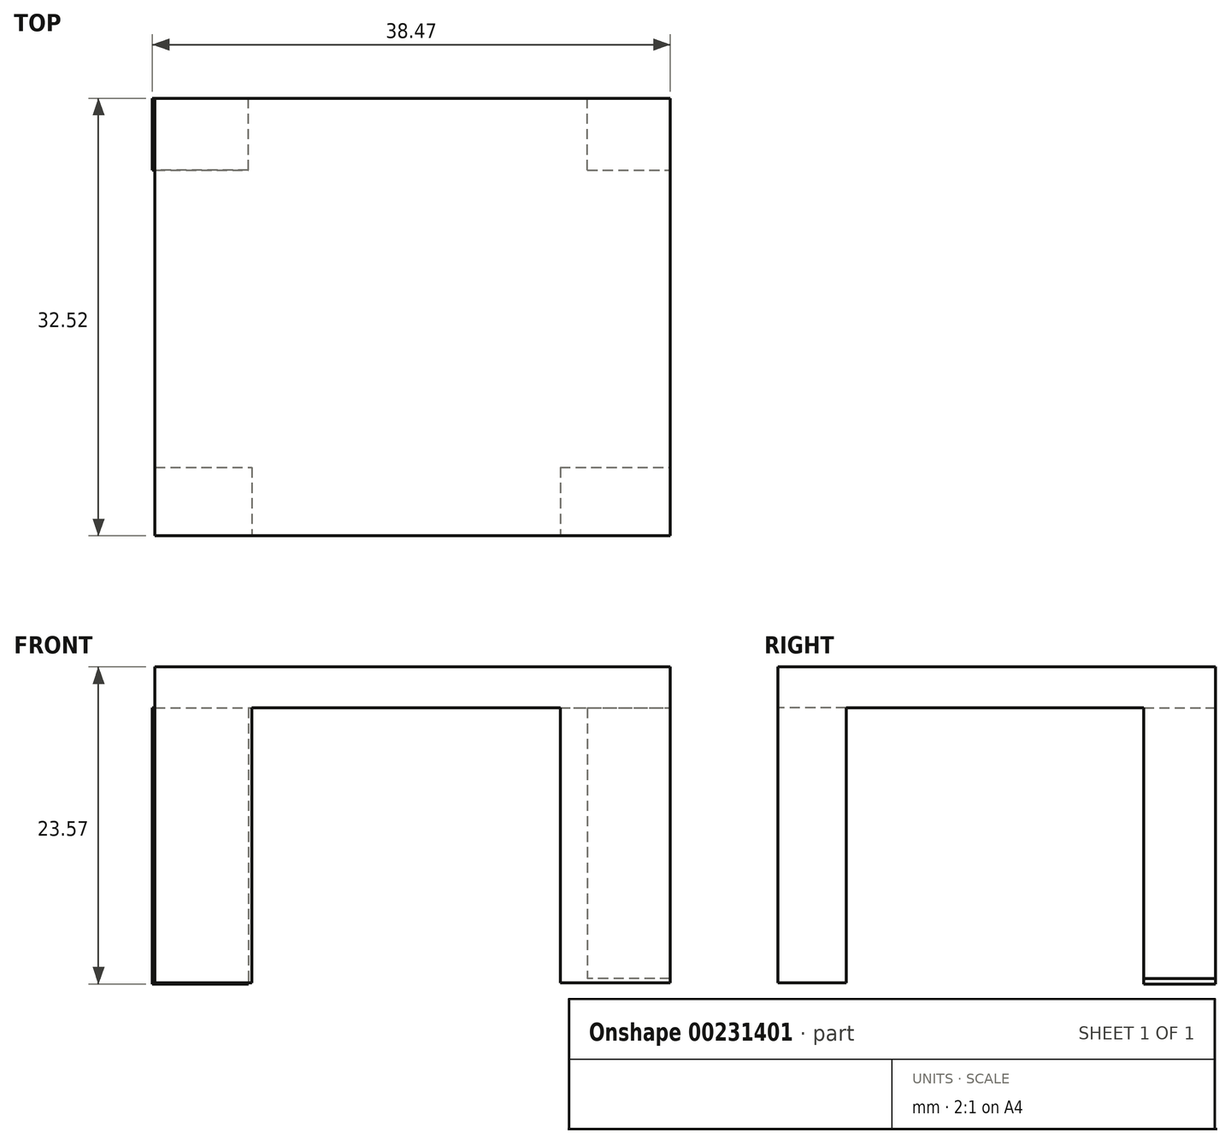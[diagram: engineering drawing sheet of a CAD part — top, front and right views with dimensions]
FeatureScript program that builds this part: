
annotation { "Feature Type Name" : "Feature", "Feature Type Description" : "" }
export const myFeature = defineFeature(function(context is Context, id is Id, definition is map)
    precondition{}
    {
        {
            var Q0;
            Q0=qCreatedBy(makeId("Top.planeOp"),FACE);
            var sketch = newSketch(context, id + "F0", { "sketchPlane" : qUnion([Q0])});
            skLineSegment(sketch, "E0.bottom", {"start": v(-51.75, -22.5) * mm, "end": v(-13.48, -22.5) * mm});
            skLineSegment(sketch, "E0.top", {"start": v(-51.75, -55.03) * mm, "end": v(-13.48, -55.03) * mm});
            skLineSegment(sketch, "E0.left", {"start": v(-51.75, -22.5) * mm, "end": v(-51.75, -55.03) * mm});
            skLineSegment(sketch, "E0.right", {"start": v(-13.48, -22.5) * mm, "end": v(-13.48, -55.03) * mm});
            skSolve(sketch);
        }
        {
            var Q0;
            Q0 = qSketchRegion(id + "F0", true);
            extrude(context, id + "F1", {"entities" : qUnion([Q0]), "depth" : 3.05 * mm});
        }
        {
            var Q0;
            Q0=makeQuery(id+"F1.opExtrude","SWEPT_FACE",FACE,{"disambiguationData":[OSD([sQuery(id+"F0.wireOp",EDGE,"E0.bottom")])]});
            var sketch = newSketch(context, id + "F2", { "sketchPlane" : qUnion([Q0])});
            skLineSegment(sketch, "E1.bottom", {"start": v(13.48, 0) * mm, "end": v(19.63, 0) * mm});
            skLineSegment(sketch, "E1.top", {"start": v(13.48, -20.13) * mm, "end": v(19.63, -20.13) * mm});
            skLineSegment(sketch, "E1.left", {"start": v(13.48, 0) * mm, "end": v(13.48, -20.13) * mm});
            skLineSegment(sketch, "E1.right", {"start": v(19.63, 0) * mm, "end": v(19.63, -20.13) * mm});
            skLineSegment(sketch, "E2.bottom", {"start": v(44.81, 0) * mm, "end": v(51.95, 0) * mm});
            skLineSegment(sketch, "E2.top", {"start": v(44.81, -20.52) * mm, "end": v(51.95, -20.52) * mm});
            skLineSegment(sketch, "E2.left", {"start": v(44.81, 0) * mm, "end": v(44.81, -20.52) * mm});
            skLineSegment(sketch, "E2.right", {"start": v(51.95, 0) * mm, "end": v(51.95, -20.52) * mm});
            skSolve(sketch);
        }
        {
            var Q0;
            Q0 = qSketchRegion(id + "F2", true);
            extrude(context, id + "F3", {"entities" : qUnion([Q0]), "operationType" : NewBodyOperationType.ADD, "oppositeDirection" : true, "depth" : 5.33 * mm});
        }
        {
            var Q0;
            Q0=makeQuery(id+"F1.opExtrude","SWEPT_FACE",FACE,{"disambiguationData":[OSD([sQuery(id+"F0.wireOp",EDGE,"E0.top")])]});
            var sketch = newSketch(context, id + "F4", { "sketchPlane" : qUnion([Q0])});
            skLineSegment(sketch, "E3.bottom", {"start": v(-51.75, 3.05) * mm, "end": v(-44.57, 3.05) * mm});
            skLineSegment(sketch, "E3.top", {"start": v(-51.75, -20.42) * mm, "end": v(-44.57, -20.42) * mm});
            skLineSegment(sketch, "E3.left", {"start": v(-51.75, 3.05) * mm, "end": v(-51.75, -20.42) * mm});
            skLineSegment(sketch, "E3.right", {"start": v(-44.57, 3.05) * mm, "end": v(-44.57, -20.42) * mm});
            skLineSegment(sketch, "E4.bottom", {"start": v(-21.65, 3.05) * mm, "end": v(-13.48, 3.05) * mm});
            skLineSegment(sketch, "E4.top", {"start": v(-21.65, -20.42) * mm, "end": v(-13.48, -20.42) * mm});
            skLineSegment(sketch, "E4.left", {"start": v(-21.65, 3.05) * mm, "end": v(-21.65, -20.42) * mm});
            skLineSegment(sketch, "E4.right", {"start": v(-13.48, 3.05) * mm, "end": v(-13.48, -20.42) * mm});
            skSolve(sketch);
        }
        {
            var Q0;
            Q0 = qSketchRegion(id + "F4", true);
            extrude(context, id + "F5", {"entities" : qUnion([Q0]), "operationType" : NewBodyOperationType.ADD, "oppositeDirection" : true, "depth" : 5.08 * mm});
        }
    });
